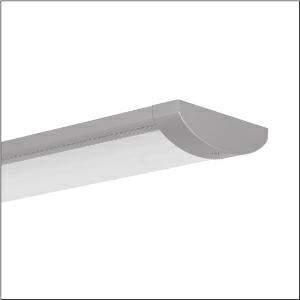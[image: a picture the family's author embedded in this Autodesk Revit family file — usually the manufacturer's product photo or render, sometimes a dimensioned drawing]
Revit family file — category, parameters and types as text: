
# Revit family: tv_20_5xa86172n0a
name_source: partatom
category: Lighting Fixtures
units: mm (PartAtom-declared; Revit-internal decimal feet)

## family parameters
Cut with Voids When Loaded = No
Host = Face
Light Source = No
Part Type = Normal
Room Calculation Point = No
Round Connector Dimension = Use Diameter
Shared = No

## types (1)
- TV 20 (1 x LED 4000K / CRI = 80 (unbekannt), 2130 lm, 4000K)
    Apparent Load = 21 VA
    CIE Flux Codes = 48 78 95 99 100
    Color Rendering = 80
    Color Temperature = 4000K
    Default Elevation = 1800 mm
    Description = TV 20, vandal-proof luminaire, primary light control with specular reflector, of aluminium, matt, primary optical cover: enclosure, of PC, frosted, light emission: direct distribution, primary light characteristic: symmetric, installation type: surface-mounted, LED, rated luminous flux: 2.130lm, luminous efficacy: 101lm/W, light colour: 840, colour temperature: 4000K, control gear: ON/OFF, mains connection: 230V, AC, 50Hz, rated input power: 21W, luminaire housing, of aluminium, coated, SITECO metallic grey (DB 702S), with wall and ceiling fixing element, length: 705mm, width: 260mm, height: 70mm, mounting height: 2.5..4.0m, protection rating (complete): IP65, insulation class (complete): insulation class I (protective earthing), certification: CE, protection symbol: F, impact resistance: 2x IK10, standard: EN 60598, packaging unit: 1 piece
    Height = 70 mm
    Lamp = 1 x LED 4000K / CRI >= 80 (unbekannt)
    Lamp Light Flux = 2130 lm
    Lamp count = 1
    Length = 705 mm
    Luminous efficacy = 101 lm/W
    Manufacturer = Siteco
    ModVariant = No
    Model = 5XA86172N0A
    Mounting Place = Ceiling
    Mounting Type = Surface mounted
    Number of Poles = 1
    OnlyDefault = Yes
    Power Factor = 1
    Product Name = TV 20
    Product group = vandal-proof luminaire
    ProductGroupID = 310
    Protection Class = Protection class I
    Protection Degree = IP 65
    RLX_Detail_Level = 1
    RLX_Emergency_Light_Flux = 0 lm
    RLX_Emergency_Type = 0
    RLX_Emergency_Type_DB = No
    RlxData = <blob elided: 34253 chars, md5=4fc259d4>
    Socket = socket
    Standby Power = 0 W
    System Light Flux = 2130 lm
    System Power = 21 W
    Type Comments = Product without accessories
    Type Image = l_1004809.jpg
    URL = http://relux.com
    VarID = ---
    Voltage = 0 V
    Weight = 0.00 kg
    Width = 260 mm

## geometry (parser evidence)
native form markers: Blend x4, Sweep x8
no freeform markers — native parametric forms only
